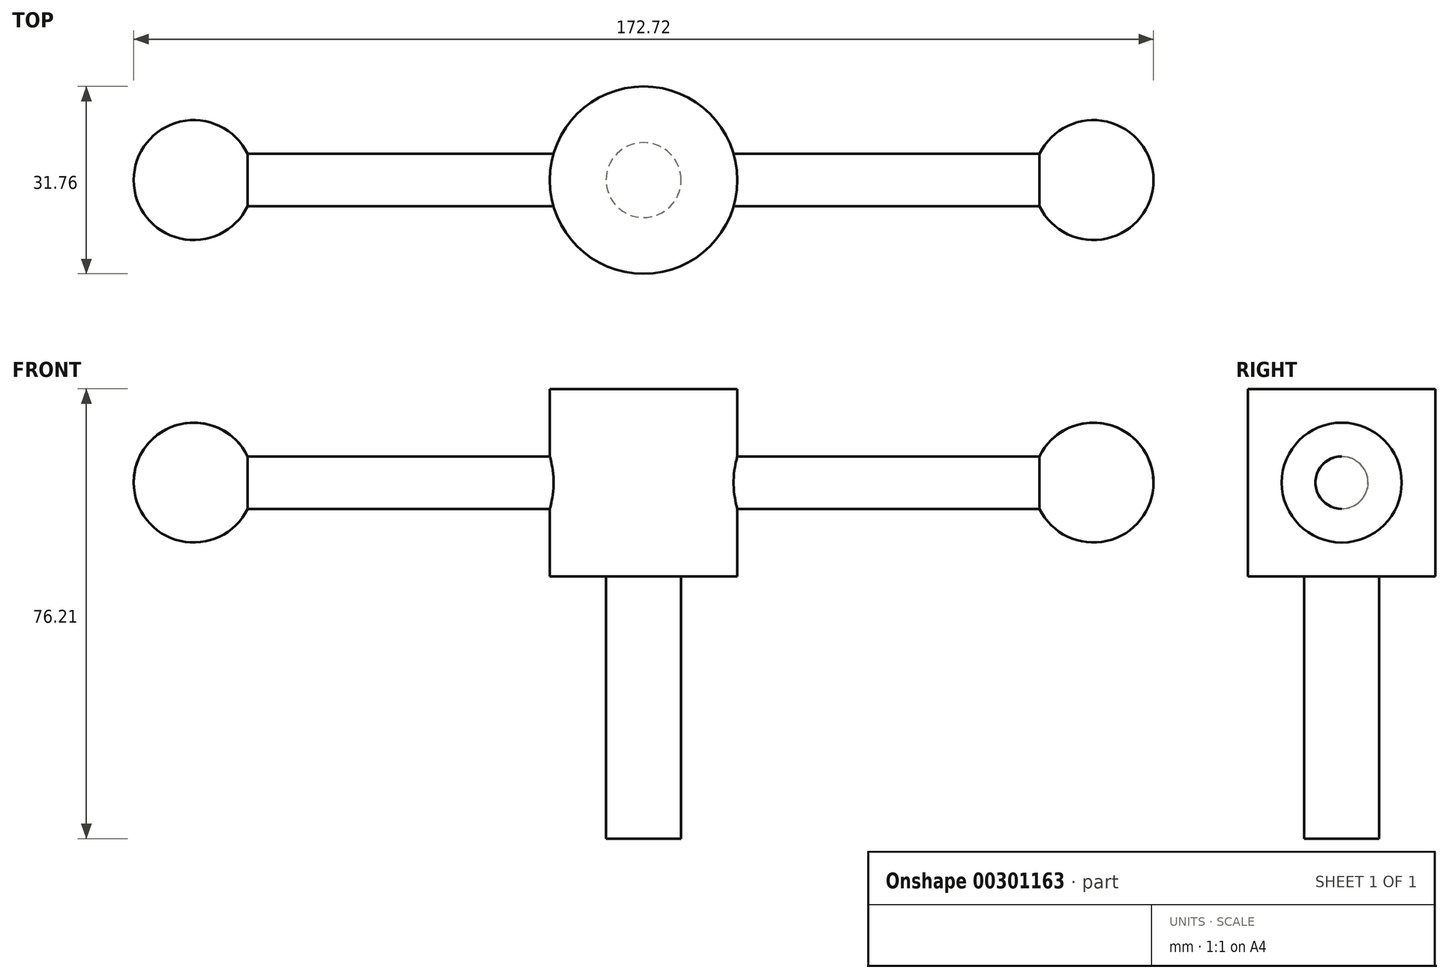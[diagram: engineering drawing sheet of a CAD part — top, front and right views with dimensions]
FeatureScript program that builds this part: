
annotation { "Feature Type Name" : "Feature", "Feature Type Description" : "" }
export const myFeature = defineFeature(function(context is Context, id is Id, definition is map)
    precondition{}
    {
        {
            var Q0;
            Q0=qCreatedBy(makeId("Top.planeOp"),FACE);
            var sketch = newSketch(context, id + "F0", { "sketchPlane" : qUnion([Q0])});
            skCircle(sketch, "E0", {"center": v(0, 0) * mm, "radius": 15.88 * mm});
            skSolve(sketch);
        }
        {
            var Q0;
            Q0 = qSketchRegion(id + "F0", true);
            extrude(context, id + "F1", {"entities" : qUnion([Q0]), "endBound" : BoundingType.SYMMETRIC, "depth" : 31.75 * mm});
        }
        {
            var Q0;
            Q0=qCreatedBy(makeId("Front.planeOp"),FACE);
            var sketch = newSketch(context, id + "F2", { "sketchPlane" : qUnion([Q0])});
            skArc(sketch, "E1", {"start": v(-67.06, 4.44) * mm, "mid": v(-78.48, 9.9) * mm, "end": v(-86.36, 0) * mm});
            skArc(sketch, "E2", {"start": v(67.06, 4.44) * mm, "mid": v(78.48, 9.9) * mm, "end": v(86.36, 0) * mm});
            skLineSegment(sketch, "E3", {"start": v(-86.36, 0) * mm, "end": v(86.36, 0) * mm});
            skLineSegment(sketch, "E4", {"start": v(-67.06, 4.44) * mm, "end": v(67.06, 4.44) * mm});
            skLineSegment(sketch, "E5", {"start": v(-102.13, 0) * mm, "end": v(110.47, 0) * mm, "construction": true});
            skSolve(sketch);
        }
        {
            var Q0;
            Q0 = qSketchRegion(id + "F2", true);
            var Q1;
            Q1=sQuery(id+"F2.wireOp",EDGE,"E5");
            revolve(context, id + "F3", {"operationType" : NewBodyOperationType.ADD, "entities" : qUnion([Q0]), "axis" : qUnion([Q1]), "revolveType" : RevolveType.FULL});
        }
        {
            var Q0;
            Q0=qCreatedBy(makeId("Top.planeOp"),FACE);
            var sketch = newSketch(context, id + "F4", { "sketchPlane" : qUnion([Q0])});
            skCircle(sketch, "E6", {"center": v(0, 0) * mm, "radius": 6.35 * mm});
            skSolve(sketch);
        }
        {
            var Q0;
            Q0 = qSketchRegion(id + "F4", true);
            extrude(context, id + "F5", {"entities" : qUnion([Q0]), "operationType" : NewBodyOperationType.ADD, "oppositeDirection" : true, "depth" : 60.32 * mm});
        }
    });
